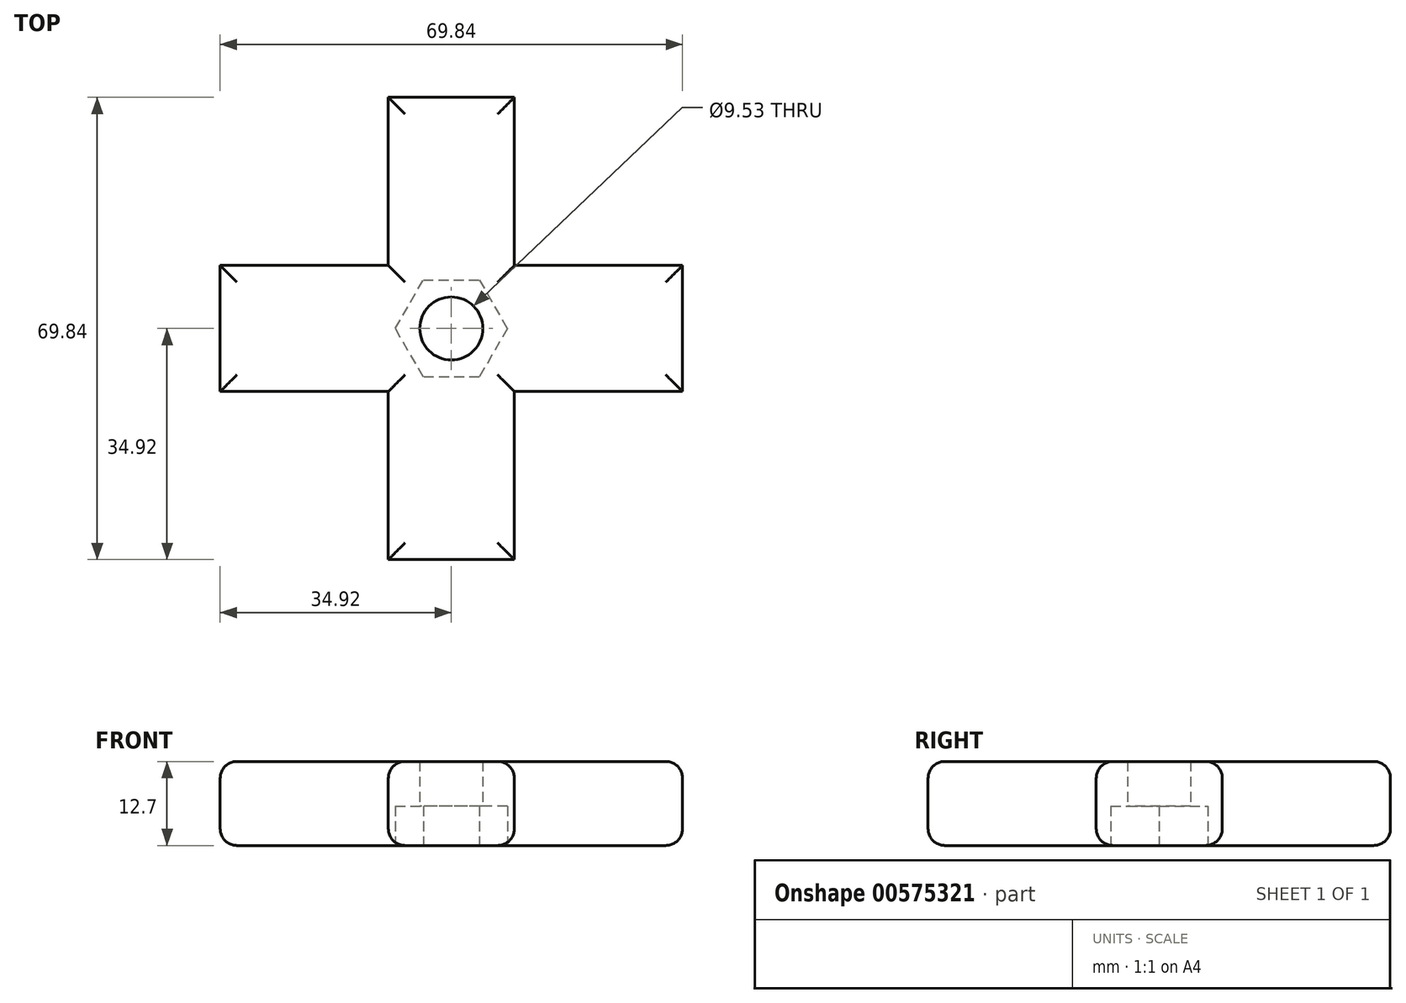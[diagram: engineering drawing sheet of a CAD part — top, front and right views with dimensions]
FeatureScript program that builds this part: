
annotation { "Feature Type Name" : "Feature", "Feature Type Description" : "" }
export const myFeature = defineFeature(function(context is Context, id is Id, definition is map)
    precondition{}
    {
        {
            var Q0;
            Q0=qCreatedBy(makeId("Top.planeOp"),FACE);
            var sketch = newSketch(context, id + "F0", { "sketchPlane" : qUnion([Q0])});
            skLineSegment(sketch, "E0.bottom", {"start": v(-9.52, 34.93) * mm, "end": v(9.53, 34.93) * mm});
            skLineSegment(sketch, "E0.top", {"start": v(-9.53, -34.93) * mm, "end": v(9.52, -34.93) * mm});
            skLineSegment(sketch, "E0.left", {"start": v(-9.52, 34.93) * mm, "end": v(-9.53, -34.93) * mm});
            skLineSegment(sketch, "E0.right", {"start": v(9.53, 34.93) * mm, "end": v(9.52, -34.93) * mm});
            skPoint(sketch, "E0.middle", {"position": v(0, 0) * mm});
            skSolve(sketch);
        }
        {
            var Q0;
            Q0=makeQuery(id+"F0.imprint","IMPRINT",FACE,{"disambiguationData":[TD([[makeQuery(id+"F0.imprint","IMPRINT",EDGE,{"derivedFrom":sQuery(id+"F0.wireOp",EDGE,"E0.bottom")}),-1.0]])]});
            extrude(context, id + "F1", {"entities" : qUnion([Q0]), "depth" : 12.7 * mm, "offsetDistance" : 25.4 * mm});
        }
        {
            var Q0;
            Q0=qCreatedBy(makeId("Top.planeOp"),FACE);
            var sketch = newSketch(context, id + "F2", { "sketchPlane" : qUnion([Q0])});
            skLineSegment(sketch, "E1.bottom", {"start": v(-34.93, 9.53) * mm, "end": v(34.93, 9.53) * mm});
            skLineSegment(sketch, "E1.top", {"start": v(-34.93, -9.53) * mm, "end": v(34.93, -9.53) * mm});
            skLineSegment(sketch, "E1.left", {"start": v(-34.93, 9.53) * mm, "end": v(-34.93, -9.53) * mm});
            skLineSegment(sketch, "E1.right", {"start": v(34.93, 9.53) * mm, "end": v(34.93, -9.53) * mm});
            skPoint(sketch, "E1.middle", {"position": v(0, 0) * mm});
            skSolve(sketch);
        }
        {
            var Q0;
            Q0=makeQuery(id+"F2.imprint","IMPRINT",FACE,{"disambiguationData":[TD([[makeQuery(id+"F2.imprint","IMPRINT",EDGE,{"derivedFrom":sQuery(id+"F2.wireOp",EDGE,"E1.bottom")}),-1.0]])]});
            extrude(context, id + "F3", {"entities" : qUnion([Q0]), "operationType" : NewBodyOperationType.ADD, "depth" : 12.7 * mm, "offsetDistance" : 25.4 * mm});
        }
        {
            var Q0;
            Q0=makeQuery(id+"F1.opExtrude","CAP_EDGE",EDGE,{"disambiguationData":[OSD([sQuery(id+"F0.wireOp",EDGE,"E0.bottom")])],"isStart":false});
            var Q1;
            {var subQ1=sQuery(id+"F0.wireOp",EDGE,"E0.left");var subQ2=sQuery(id+"F0.wireOp",EDGE,"E0.bottom");Q1=makeQuery(id+"F3.boolean.opBoolean","SPLIT",EDGE,{"disambiguationData":[TD([makeQuery(id+"F1.opExtrude","SWEPT_FACE",FACE,{"disambiguationData":[OSD([subQ2])]})])],"derivedFrom":makeQuery(id+"F1.opExtrude","CAP_EDGE",EDGE,{"disambiguationData":[OSD([subQ1])],"isStart":false})});}
            var Q2;
            {var subQ1=sQuery(id+"F0.wireOp",EDGE,"E0.right");var subQ2=sQuery(id+"F0.wireOp",EDGE,"E0.bottom");Q2=makeQuery(id+"F3.boolean.opBoolean","SPLIT",EDGE,{"disambiguationData":[TD([makeQuery(id+"F1.opExtrude","SWEPT_FACE",FACE,{"disambiguationData":[OSD([subQ2])]})])],"derivedFrom":makeQuery(id+"F1.opExtrude","CAP_EDGE",EDGE,{"disambiguationData":[OSD([subQ1])],"isStart":false})});}
            var Q3;
            Q3=makeQuery(id+"F3.boolean.opBoolean","MERGE",FACE,{"derivedFrom":[makeQuery(id+"F1.opExtrude","CAP_FACE",FACE,{"disambiguationData":[OSD([sQuery(id+"F0.wireOp",EDGE,"E0.bottom"),sQuery(id+"F0.wireOp",EDGE,"E0.top"),sQuery(id+"F0.wireOp",EDGE,"E0.left"),sQuery(id+"F0.wireOp",EDGE,"E0.right")])],"isStart":false}),makeQuery(id+"F3.opExtrude","CAP_FACE",FACE,{"disambiguationData":[OSD([sQuery(id+"F2.wireOp",EDGE,"E1.bottom"),sQuery(id+"F2.wireOp",EDGE,"E1.top"),sQuery(id+"F2.wireOp",EDGE,"E1.left"),sQuery(id+"F2.wireOp",EDGE,"E1.right")])],"isStart":false})]});
            fillet(context, id + "F4", {"entities" : qUnion([Q0, Q1, Q2, Q3]), "radius" : 2.54 * mm, "tangentPropagation" : true, "allowEdgeOverflow" : false});
        }
        {
            var Q0;
            {var subQ1=sQuery(id+"F0.wireOp",EDGE,"E0.left");var subQ2=sQuery(id+"F0.wireOp",EDGE,"E0.top");Q0=makeQuery(id+"F3.boolean.opBoolean","SPLIT",EDGE,{"disambiguationData":[TD([makeQuery(id+"F1.opExtrude","SWEPT_FACE",FACE,{"disambiguationData":[OSD([subQ2])]})])],"derivedFrom":makeQuery(id+"F1.opExtrude","CAP_EDGE",EDGE,{"disambiguationData":[OSD([subQ1])],"isStart":true})});}
            var Q1;
            Q1=makeQuery(id+"F1.opExtrude","CAP_EDGE",EDGE,{"disambiguationData":[OSD([sQuery(id+"F0.wireOp",EDGE,"E0.top")])],"isStart":true});
            var Q2;
            {var subQ1=sQuery(id+"F0.wireOp",EDGE,"E0.right");var subQ2=sQuery(id+"F0.wireOp",EDGE,"E0.top");Q2=makeQuery(id+"F3.boolean.opBoolean","SPLIT",EDGE,{"disambiguationData":[TD([makeQuery(id+"F1.opExtrude","SWEPT_FACE",FACE,{"disambiguationData":[OSD([subQ2])]})])],"derivedFrom":makeQuery(id+"F1.opExtrude","CAP_EDGE",EDGE,{"disambiguationData":[OSD([subQ1])],"isStart":true})});}
            var Q3;
            Q3=makeQuery(id+"F3.boolean.opBoolean","MERGE",FACE,{"derivedFrom":[makeQuery(id+"F1.opExtrude","CAP_FACE",FACE,{"disambiguationData":[OSD([sQuery(id+"F0.wireOp",EDGE,"E0.bottom"),sQuery(id+"F0.wireOp",EDGE,"E0.top"),sQuery(id+"F0.wireOp",EDGE,"E0.left"),sQuery(id+"F0.wireOp",EDGE,"E0.right")])],"isStart":true}),makeQuery(id+"F3.opExtrude","CAP_FACE",FACE,{"disambiguationData":[OSD([sQuery(id+"F2.wireOp",EDGE,"E1.bottom"),sQuery(id+"F2.wireOp",EDGE,"E1.top"),sQuery(id+"F2.wireOp",EDGE,"E1.left"),sQuery(id+"F2.wireOp",EDGE,"E1.right")])],"isStart":true})]});
            fillet(context, id + "F5", {"entities" : qUnion([Q0, Q1, Q2, Q3]), "radius" : 2.54 * mm, "tangentPropagation" : true, "allowEdgeOverflow" : false});
        }
        {
            var Q0;
            Q0=qCreatedBy(makeId("Top.planeOp"),FACE);
            var sketch = newSketch(context, id + "F6", { "sketchPlane" : qUnion([Q0])});
            skCircle(sketch, "E2.cCircle", {"center": v(0, 0) * mm, "radius": 7.33 * mm, "construction": true});
            skLineSegment(sketch, "E2.0", {"start": v(-8.46, 0) * mm, "end": v(-4.23, 7.33) * mm});
            skLineSegment(sketch, "E2.1", {"start": v(-4.23, 7.33) * mm, "end": v(4.23, 7.33) * mm});
            skLineSegment(sketch, "E2.2", {"start": v(4.23, 7.33) * mm, "end": v(8.46, 0) * mm});
            skLineSegment(sketch, "E2.3", {"start": v(8.46, 0) * mm, "end": v(4.23, -7.33) * mm});
            skLineSegment(sketch, "E2.4", {"start": v(4.23, -7.33) * mm, "end": v(-4.23, -7.33) * mm});
            skLineSegment(sketch, "E2.5", {"start": v(-4.23, -7.33) * mm, "end": v(-8.46, 0) * mm});
            skPoint(sketch, "E2.0.midPoint", {"position": v(-6.35, 3.66) * mm});
            skSolve(sketch);
        }
        {
            var Q0;
            Q0 = qSketchRegion(id + "F6", true);
            extrude(context, id + "F7", {"entities" : qUnion([Q0]), "operationType" : NewBodyOperationType.REMOVE, "depth" : 5.94 * mm, "offsetDistance" : 25.4 * mm});
        }
        {
            var Q0;
            Q0=qCreatedBy(makeId("Top.planeOp"),FACE);
            var sketch = newSketch(context, id + "F8", { "sketchPlane" : qUnion([Q0])});
            skCircle(sketch, "E3", {"center": v(0, 0) * mm, "radius": 4.76 * mm});
            skSolve(sketch);
        }
        {
            var Q0;
            Q0=sQuery(id+"F8.wireOp",VERTEX,"E3.center");
            var Q1;
            Q1=makeQuery(id+"F1.opExtrude","SWEPT_BODY",BODY,{"disambiguationData":[OSD([sQuery(id+"F0.wireOp",EDGE,"E0.bottom"),sQuery(id+"F0.wireOp",EDGE,"E0.top"),sQuery(id+"F0.wireOp",EDGE,"E0.left"),sQuery(id+"F0.wireOp",EDGE,"E0.right")])]});
            hole(context, id + "F9", {"style" : HoleStyle.SIMPLE, "endStyle" : HoleEndStyle.THROUGH, "oppositeDirection" : true, "holeDiameter" : 9.52 * mm, "majorDiameter" : 6.35 * mm, "isTappedThrough" : true, "tappedDepth" : 12.7 * mm, "tapClearance" : 3, "locations" : qUnion([Q0]), "scope" : qUnion([Q1])});
        }
    });
